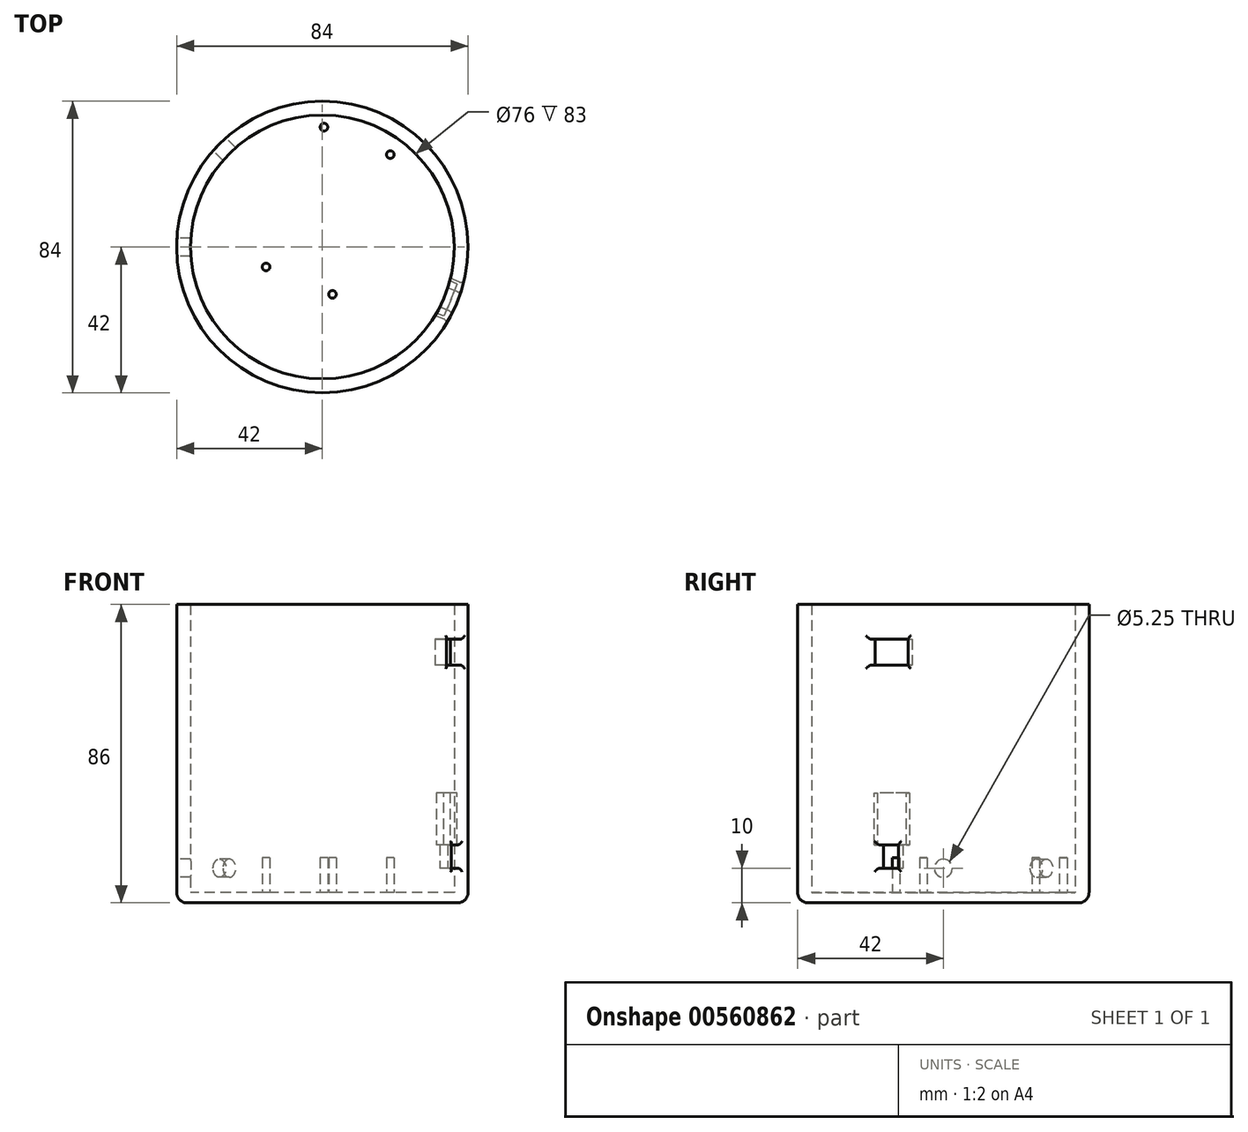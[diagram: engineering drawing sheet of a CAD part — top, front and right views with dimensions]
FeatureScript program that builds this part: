
annotation { "Feature Type Name" : "Feature", "Feature Type Description" : "" }
export const myFeature = defineFeature(function(context is Context, id is Id, definition is map)
    precondition{}
    {
        {
            var Q0;
            Q0=qCreatedBy(makeId("Top.planeOp"),FACE);
            var sketch = newSketch(context, id + "F0", { "sketchPlane" : qUnion([Q0])});
            skCircle(sketch, "E0", {"center": v(0, 0) * mm, "radius": 42 * mm});
            skCircle(sketch, "E1", {"center": v(0, 0) * mm, "radius": 38 * mm});
            skPoint(sketch, "E2", {"position": v(-42, 0) * mm});
            skPoint(sketch, "E3", {"position": v(-29.7, 29.7) * mm});
            skLineSegment(sketch, "E4", {"start": v(-42, 0) * mm, "end": v(0, 0) * mm, "construction": true});
            skLineSegment(sketch, "E5", {"start": v(-29.7, 29.7) * mm, "end": v(0, 0) * mm, "construction": true});
            skLineSegment(sketch, "E6", {"start": v(0, 0) * mm, "end": v(29.7, 29.7) * mm, "construction": true});
            skLineSegment(sketch, "E7", {"start": v(0, 0) * mm, "end": v(-29.7, -29.7) * mm, "construction": true});
            skPoint(sketch, "E8", {"position": v(-38.8, 16.07) * mm});
            skLineSegment(sketch, "E9", {"start": v(0, 0) * mm, "end": v(-38.8, 16.07) * mm, "construction": true});
            skLineSegment(sketch, "E10", {"start": v(-29.7, 29.7) * mm, "end": v(-42, 0) * mm, "construction": true});
            skSolve(sketch);
        }
        {
            var Q0;
            Q0=makeQuery(id+"F0.imprint","IMPRINT",FACE,{"disambiguationData":[TD([[makeQuery(id+"F0.imprint","IMPRINT",EDGE,{"derivedFrom":sQuery(id+"F0.wireOp",EDGE,"E0")}),1.0]])]});
            extrude(context, id + "F1", {"entities" : qUnion([Q0]), "depth" : 86 * mm, "offsetDistance" : 25 * mm});
        }
        {
            var Q0;
            Q0=makeQuery(id+"F0.imprint","IMPRINT",FACE,{"disambiguationData":[TD([[makeQuery(id+"F0.imprint","IMPRINT",EDGE,{"derivedFrom":sQuery(id+"F0.wireOp",EDGE,"E0")}),1.0]])]});
            var Q1;
            Q1=makeQuery(id+"F0.imprint","IMPRINT",FACE,{"disambiguationData":[TD([[makeQuery(id+"F0.imprint","IMPRINT",EDGE,{"derivedFrom":sQuery(id+"F0.wireOp",EDGE,"E1")}),1.0]])]});
            extrude(context, id + "F2", {"entities" : qUnion([Q0, Q1]), "operationType" : NewBodyOperationType.ADD, "depth" : 3 * mm, "offsetDistance" : 25 * mm});
        }
        {
            var Q0;
            Q0=sQuery(id+"F0.wireOp",VERTEX,"E2");
            var Q1;
            Q1=qCreatedBy(makeId("Right.planeOp"),FACE);
            cPlane(context, id + "F3", {"entities" : qUnion([Q0, Q1]), "cplaneType" : CPlaneType.PLANE_POINT, "offset" : 25 * mm, "width" : 150 * mm, "height" : 150 * mm});
        }
        {
            var Q0;
            Q0=sQuery(id+"F0.wireOp",VERTEX,"E3");
            var Q1;
            Q1=sQuery(id+"F0.wireOp",EDGE,"E6");
            cPlane(context, id + "F4", {"entities" : qUnion([Q0, Q1]), "cplaneType" : CPlaneType.CURVE_POINT, "offset" : 25 * mm, "width" : 150 * mm, "height" : 150 * mm});
        }
        {
            var Q0;
            Q0=qCreatedBy(makeId("Right.planeOp"),FACE);
            var Q1;
            Q1=qCreatedBy(makeId("Front.planeOp"),FACE);
            cPlane(context, id + "F5", {"entities" : qUnion([Q0, Q1]), "cplaneType" : CPlaneType.MID_PLANE, "offset" : 25 * mm, "flipAlignment" : true, "width" : 150 * mm, "height" : 150 * mm});
        }
        {
            var Q0;
            Q0=sQuery(id+"F0.wireOp",VERTEX,"E3");
            var Q1;
            Q1=qCreatedBy(id+"F5.planeOp",FACE);
            cPlane(context, id + "F6", {"entities" : qUnion([Q0, Q1]), "cplaneType" : CPlaneType.PLANE_POINT, "offset" : 25 * mm, "width" : 150 * mm, "height" : 150 * mm});
        }
        {
            var Q0;
            Q0=qCreatedBy(id+"F3.planeOp",FACE);
            var sketch = newSketch(context, id + "F7", { "sketchPlane" : qUnion([Q0])});
            skCircle(sketch, "E11", {"center": v(0, 10) * mm, "radius": 2.62 * mm});
            skSolve(sketch);
        }
        {
            var Q0;
            Q0=makeQuery(id+"F7.imprint","IMPRINT",FACE,{"disambiguationData":[TD([[makeQuery(id+"F7.imprint","IMPRINT",EDGE,{"derivedFrom":sQuery(id+"F7.wireOp",EDGE,"E11")}),1.0]])]});
            extrude(context, id + "F8", {"entities" : qUnion([Q0]), "operationType" : NewBodyOperationType.REMOVE, "endBound" : BoundingType.UP_TO_NEXT, "depth" : 25 * mm, "offsetDistance" : 25 * mm});
        }
        {
            var Q0;
            Q0=qCreatedBy(id+"F6.planeOp",FACE);
            var sketch = newSketch(context, id + "F9", { "sketchPlane" : qUnion([Q0])});
            skCircle(sketch, "E12", {"center": v(0, 10) * mm, "radius": 2.62 * mm});
            skSolve(sketch);
        }
        {
            var Q0;
            Q0 = qSketchRegion(id + "F9", true);
            extrude(context, id + "F10", {"entities" : qUnion([Q0]), "operationType" : NewBodyOperationType.REMOVE, "endBound" : BoundingType.UP_TO_NEXT, "depth" : 25 * mm, "offsetDistance" : 25 * mm});
        }
        {
            var Q0;
            Q0=makeQuery(id+"F1.opExtrude","CAP_EDGE",EDGE,{"disambiguationData":[OSD([sQuery(id+"F0.wireOp",EDGE,"E0")])],"isStart":true});
            fillet(context, id + "F11", {"entities" : qUnion([Q0]), "radius" : 3 * mm, "tangentPropagation" : true, "allowEdgeOverflow" : false});
        }
        {
            var Q0;
            Q0=qCreatedBy(makeId("Front.planeOp"),FACE);
            var Q1;
            Q1=qCreatedBy(id+"F4.planeOp",FACE);
            cPlane(context, id + "F12", {"entities" : qUnion([Q0, Q1]), "cplaneType" : CPlaneType.MID_PLANE, "offset" : 25 * mm, "width" : 150 * mm, "height" : 150 * mm});
        }
        {
            var Q0;
            Q0=qCreatedBy(id+"F5.planeOp",FACE);
            var Q1;
            Q1=qCreatedBy(makeId("Right.planeOp"),FACE);
            cPlane(context, id + "F13", {"entities" : qUnion([Q0, Q1]), "cplaneType" : CPlaneType.MID_PLANE, "offset" : 25 * mm, "flipAlignment" : true, "width" : 150 * mm, "height" : 150 * mm});
        }
        {
            var Q0;
            Q0=qCreatedBy(id+"F13.planeOp",FACE);
            var sketch = newSketch(context, id + "F14", { "sketchPlane" : qUnion([Q0])});
            skLineSegment(sketch, "E13.right", {"start": v(-5.8, 76) * mm, "end": v(-5.8, 68.5) * mm});
            skLineSegment(sketch, "E14.right", {"start": v(5.8, 68.5) * mm, "end": v(5.8, 76) * mm});
            skLineSegment(sketch, "E15", {"start": v(5.8, 68.5) * mm, "end": v(-5.8, 68.5) * mm});
            skLineSegment(sketch, "E16", {"start": v(-5.8, 76) * mm, "end": v(5.8, 76) * mm});
            skLineSegment(sketch, "E17.bottom", {"start": v(3, 10) * mm, "end": v(-3, 10) * mm});
            skLineSegment(sketch, "E17.top", {"start": v(3, 16.7) * mm, "end": v(-3, 16.7) * mm});
            skLineSegment(sketch, "E17.left", {"start": v(3, 10) * mm, "end": v(3, 16.7) * mm});
            skLineSegment(sketch, "E17.right", {"start": v(-3, 10) * mm, "end": v(-3, 16.7) * mm});
            skLineSegment(sketch, "E18.bottom", {"start": v(5, 16.7) * mm, "end": v(-5, 16.7) * mm});
            skLineSegment(sketch, "E18.top", {"start": v(5, 31.7) * mm, "end": v(-5, 31.7) * mm});
            skLineSegment(sketch, "E18.left", {"start": v(5, 16.7) * mm, "end": v(5, 31.7) * mm});
            skLineSegment(sketch, "E18.right", {"start": v(-5, 16.7) * mm, "end": v(-5, 31.7) * mm});
            skSolve(sketch);
        }
        {
            var Q0;
            Q0=makeQuery(id+"F14.imprint","IMPRINT",FACE,{"disambiguationData":[TD([[makeQuery(id+"F14.imprint","IMPRINT",EDGE,{"derivedFrom":sQuery(id+"F14.wireOp",EDGE,"E13.right")}),1.0]])]});
            var Q1;
            Q1=makeQuery(id+"F14.imprint","IMPRINT",FACE,{"disambiguationData":[TD([[makeQuery(id+"F14.imprint","IMPRINT",EDGE,{"derivedFrom":sQuery(id+"F14.wireOp",EDGE,"E17.bottom")}),-1.0]])]});
            extrude(context, id + "F15", {"entities" : qUnion([Q0, Q1]), "operationType" : NewBodyOperationType.REMOVE, "endBound" : BoundingType.THROUGH_ALL, "depth" : 25 * mm, "offsetDistance" : 25 * mm});
        }
        {
            var Q0;
            Q0=makeQuery(id+"F2.opExtrude","CAP_FACE",FACE,{"disambiguationData":[OSD([sQuery(id+"F0.wireOp",EDGE,"E0")])],"isStart":false});
            var sketch = newSketch(context, id + "F16", { "sketchPlane" : qUnion([Q0])});
            skCircle(sketch, "E19", {"center": v(-16.23, -5.73) * mm, "radius": 1.1 * mm});
            skCircle(sketch, "E20", {"center": v(0.46, 34.56) * mm, "radius": 1.1 * mm});
            skCircle(sketch, "E21", {"center": v(19.58, 26.63) * mm, "radius": 1.1 * mm});
            skCircle(sketch, "E22", {"center": v(2.9, -13.65) * mm, "radius": 1.1 * mm});
            skSolve(sketch);
        }
        {
            var Q0;
            Q0=makeQuery(id+"F16.imprint","IMPRINT",FACE,{"disambiguationData":[TD([[makeQuery(id+"F16.imprint","IMPRINT",EDGE,{"derivedFrom":sQuery(id+"F16.wireOp",EDGE,"E21")}),1.0]])]});
            var Q1;
            Q1=makeQuery(id+"F16.imprint","IMPRINT",FACE,{"disambiguationData":[TD([[makeQuery(id+"F16.imprint","IMPRINT",EDGE,{"derivedFrom":sQuery(id+"F16.wireOp",EDGE,"E22")}),1.0]])]});
            var Q2;
            Q2=makeQuery(id+"F16.imprint","IMPRINT",FACE,{"disambiguationData":[TD([[makeQuery(id+"F16.imprint","IMPRINT",EDGE,{"derivedFrom":sQuery(id+"F16.wireOp",EDGE,"E19")}),1.0]])]});
            var Q3;
            Q3=makeQuery(id+"F16.imprint","IMPRINT",FACE,{"disambiguationData":[TD([[makeQuery(id+"F16.imprint","IMPRINT",EDGE,{"derivedFrom":sQuery(id+"F16.wireOp",EDGE,"E20")}),1.0]])]});
            extrude(context, id + "F17", {"entities" : qUnion([Q0, Q1, Q2, Q3]), "operationType" : NewBodyOperationType.ADD, "depth" : 10 * mm, "offsetDistance" : 25 * mm});
        }
        {
            var Q0;
            Q0=makeQuery(id+"F15.boolean.opBoolean","INTERSECT",EDGE,{"derivedFrom":[makeQuery(id+"F1.opExtrude","SWEPT_FACE",FACE,{"disambiguationData":[OSD([sQuery(id+"F0.wireOp",EDGE,"E0")])]}),makeQuery(id+"F15.opExtrude","SWEPT_FACE",FACE,{"disambiguationData":[OSD([sQuery(id+"F14.wireOp",EDGE,"E15")])]})]});
            var Q1;
            Q1=makeQuery(id+"F15.boolean.opBoolean","INTERSECT",EDGE,{"derivedFrom":[makeQuery(id+"F1.opExtrude","SWEPT_FACE",FACE,{"disambiguationData":[OSD([sQuery(id+"F0.wireOp",EDGE,"E0")])]}),makeQuery(id+"F15.opExtrude","SWEPT_FACE",FACE,{"disambiguationData":[OSD([sQuery(id+"F14.wireOp",EDGE,"E13.right")])]})]});
            var Q2;
            Q2=makeQuery(id+"F15.boolean.opBoolean","INTERSECT",EDGE,{"derivedFrom":[makeQuery(id+"F1.opExtrude","SWEPT_FACE",FACE,{"disambiguationData":[OSD([sQuery(id+"F0.wireOp",EDGE,"E0")])]}),makeQuery(id+"F15.opExtrude","SWEPT_FACE",FACE,{"disambiguationData":[OSD([sQuery(id+"F14.wireOp",EDGE,"E16")])]})]});
            var Q3;
            Q3=makeQuery(id+"F15.boolean.opBoolean","INTERSECT",EDGE,{"derivedFrom":[makeQuery(id+"F1.opExtrude","SWEPT_FACE",FACE,{"disambiguationData":[OSD([sQuery(id+"F0.wireOp",EDGE,"E0")])]}),makeQuery(id+"F15.opExtrude","SWEPT_FACE",FACE,{"disambiguationData":[OSD([sQuery(id+"F14.wireOp",EDGE,"E14.right")])]})]});
            var Q4;
            Q4=makeQuery(id+"F15.boolean.opBoolean","INTERSECT",EDGE,{"derivedFrom":[makeQuery(id+"F1.opExtrude","SWEPT_FACE",FACE,{"disambiguationData":[OSD([sQuery(id+"F0.wireOp",EDGE,"E0")])]}),makeQuery(id+"F15.opExtrude","SWEPT_FACE",FACE,{"disambiguationData":[OSD([sQuery(id+"F14.wireOp",EDGE,"E17.bottom")])]})]});
            var Q5;
            Q5=makeQuery(id+"F15.boolean.opBoolean","INTERSECT",EDGE,{"derivedFrom":[makeQuery(id+"F1.opExtrude","SWEPT_FACE",FACE,{"disambiguationData":[OSD([sQuery(id+"F0.wireOp",EDGE,"E0")])]}),makeQuery(id+"F15.opExtrude","SWEPT_FACE",FACE,{"disambiguationData":[OSD([sQuery(id+"F14.wireOp",EDGE,"E17.left")])]})]});
            var Q6;
            Q6=makeQuery(id+"F15.boolean.opBoolean","INTERSECT",EDGE,{"derivedFrom":[makeQuery(id+"F1.opExtrude","SWEPT_FACE",FACE,{"disambiguationData":[OSD([sQuery(id+"F0.wireOp",EDGE,"E0")])]}),makeQuery(id+"F15.opExtrude","SWEPT_FACE",FACE,{"disambiguationData":[OSD([sQuery(id+"F14.wireOp",EDGE,"E17.top")])]})]});
            var Q7;
            Q7=makeQuery(id+"F15.boolean.opBoolean","INTERSECT",EDGE,{"derivedFrom":[makeQuery(id+"F1.opExtrude","SWEPT_FACE",FACE,{"disambiguationData":[OSD([sQuery(id+"F0.wireOp",EDGE,"E0")])]}),makeQuery(id+"F15.opExtrude","SWEPT_FACE",FACE,{"disambiguationData":[OSD([sQuery(id+"F14.wireOp",EDGE,"E17.right")])]})]});
            fillet(context, id + "F18", {"entities" : qUnion([Q0, Q1, Q2, Q3, Q4, Q5, Q6, Q7]), "radius" : 1 * mm, "tangentPropagation" : true, "allowEdgeOverflow" : false});
        }
        {
            var Q0;
            Q0=makeQuery(id+"F14.imprint","IMPRINT",FACE,{"disambiguationData":[TD([[makeQuery(id+"F14.imprint","IMPRINT",EDGE,{"derivedFrom":sQuery(id+"F14.wireOp",EDGE,"E18.top")}),1.0]])]});
            extrude(context, id + "F19", {"entities" : qUnion([Q0]), "operationType" : NewBodyOperationType.REMOVE, "depth" : 40 * mm, "offsetDistance" : 25 * mm});
        }
    });
